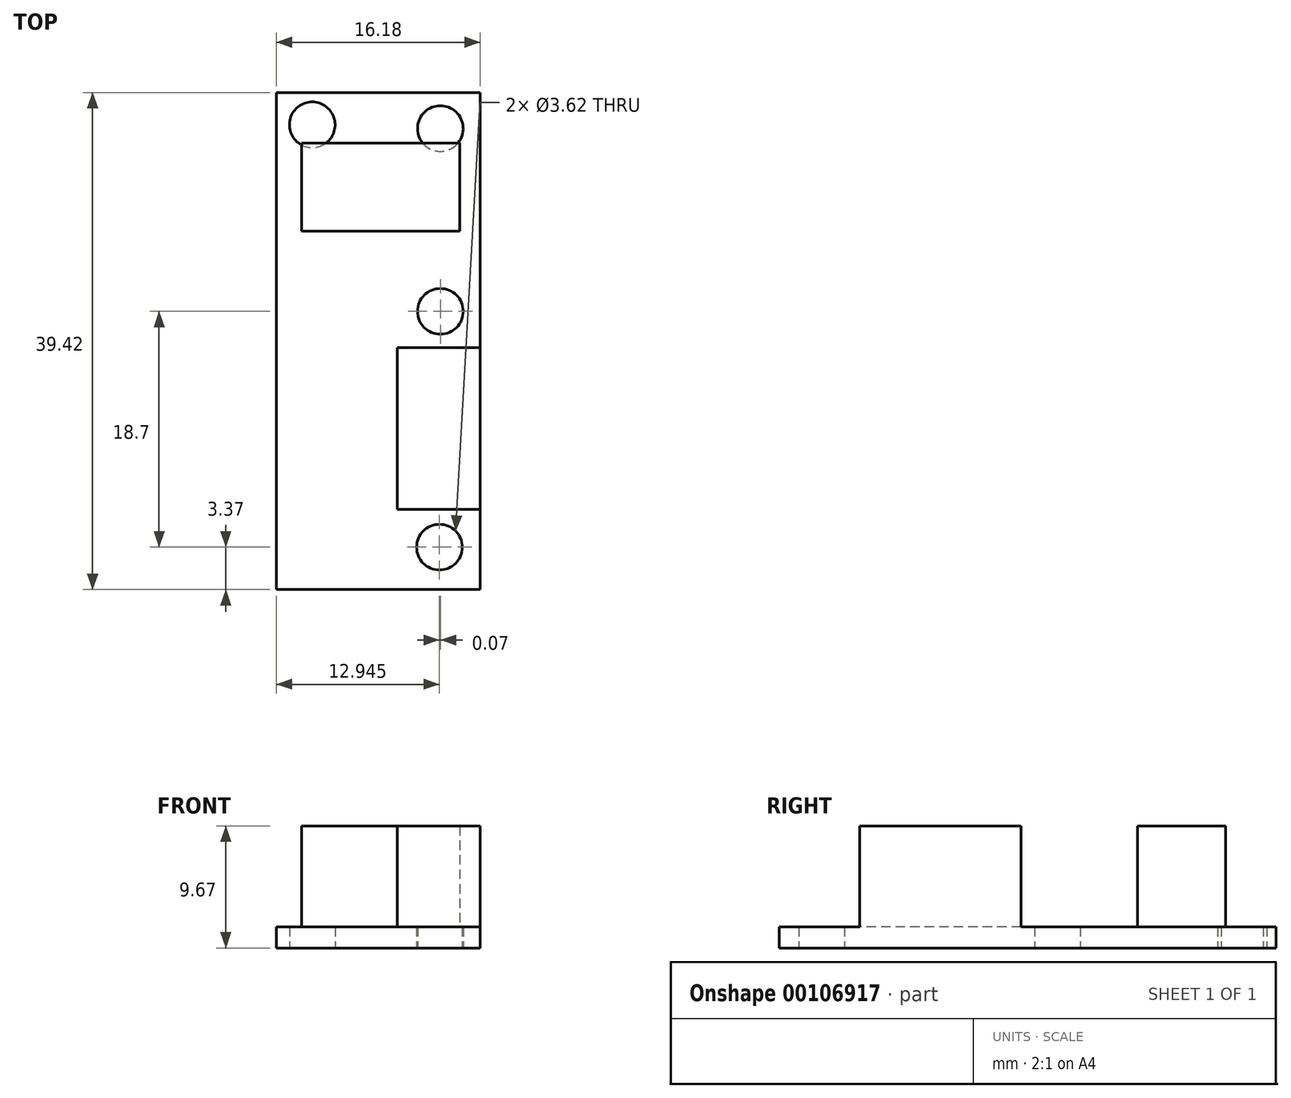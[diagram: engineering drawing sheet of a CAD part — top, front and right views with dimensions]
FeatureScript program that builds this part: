
annotation { "Feature Type Name" : "Feature", "Feature Type Description" : "" }
export const myFeature = defineFeature(function(context is Context, id is Id, definition is map)
    precondition{}
    {
        {
            var Q0;
            Q0=qCreatedBy(makeId("Top.planeOp"),FACE);
            var sketch = newSketch(context, id + "F0", { "sketchPlane" : qUnion([Q0])});
            skLineSegment(sketch, "E0.bottom", {"start": v(8.08, -19.71) * mm, "end": v(-8.09, -19.71) * mm});
            skLineSegment(sketch, "E0.top", {"start": v(8.09, 19.71) * mm, "end": v(-8.08, 19.71) * mm});
            skLineSegment(sketch, "E0.left", {"start": v(8.08, -19.71) * mm, "end": v(8.09, 19.7) * mm});
            skLineSegment(sketch, "E0.right", {"start": v(-8.09, -19.71) * mm, "end": v(-8.08, 19.7) * mm});
            skPoint(sketch, "E0.middle", {"position": v(0, 0) * mm});
            skCircle(sketch, "E1", {"center": v(-5.23, 17.16) * mm, "radius": 1.81 * mm});
            skCircle(sketch, "E2", {"center": v(4.93, 2.36) * mm, "radius": 1.81 * mm});
            skCircle(sketch, "E3", {"center": v(4.92, 16.86) * mm, "radius": 1.81 * mm});
            skCircle(sketch, "E4", {"center": v(4.85, -16.34) * mm, "radius": 1.81 * mm});
            skSolve(sketch);
        }
        {
            var Q0;
            Q0 = qSketchRegion(id + "F0", true);
            extrude(context, id + "F1", {"entities" : qUnion([Q0]), "depth" : 1.67 * mm});
        }
        {
            var Q0;
            Q0=makeQuery(id+"F1.opExtrude","CAP_FACE",FACE,{"disambiguationData":[OSD([sQuery(id+"F0.wireOp",EDGE,"E0.bottom"),sQuery(id+"F0.wireOp",EDGE,"E0.top"),sQuery(id+"F0.wireOp",EDGE,"E0.left"),sQuery(id+"F0.wireOp",EDGE,"E0.right"),sQuery(id+"F0.wireOp",EDGE,"E1"),sQuery(id+"F0.wireOp",EDGE,"E2"),sQuery(id+"F0.wireOp",EDGE,"E3"),sQuery(id+"F0.wireOp",EDGE,"E4")])],"isStart":false});
            var sketch = newSketch(context, id + "F2", { "sketchPlane" : qUnion([Q0])});
            skLineSegment(sketch, "E5.bottom", {"start": v(8.09, -0.52) * mm, "end": v(1.52, -0.52) * mm});
            skLineSegment(sketch, "E5.top", {"start": v(8.09, -13.33) * mm, "end": v(1.53, -13.33) * mm});
            skLineSegment(sketch, "E5.left", {"start": v(8.09, -0.52) * mm, "end": v(8.09, -13.33) * mm});
            skLineSegment(sketch, "E5.right", {"start": v(1.52, -0.52) * mm, "end": v(1.53, -13.33) * mm});
            skLineSegment(sketch, "E6.bottom", {"start": v(-6.08, 15.71) * mm, "end": v(6.46, 15.71) * mm});
            skLineSegment(sketch, "E6.top", {"start": v(-6.08, 8.71) * mm, "end": v(6.46, 8.71) * mm});
            skLineSegment(sketch, "E6.left", {"start": v(-6.08, 15.71) * mm, "end": v(-6.08, 8.71) * mm});
            skLineSegment(sketch, "E6.right", {"start": v(6.47, 15.71) * mm, "end": v(6.47, 8.71) * mm});
            skSolve(sketch);
        }
        {
            var Q0;
            Q0 = qSketchRegion(id + "F2", true);
            extrude(context, id + "F3", {"entities" : qUnion([Q0]), "operationType" : NewBodyOperationType.ADD, "depth" : 8 * mm});
        }
    });
